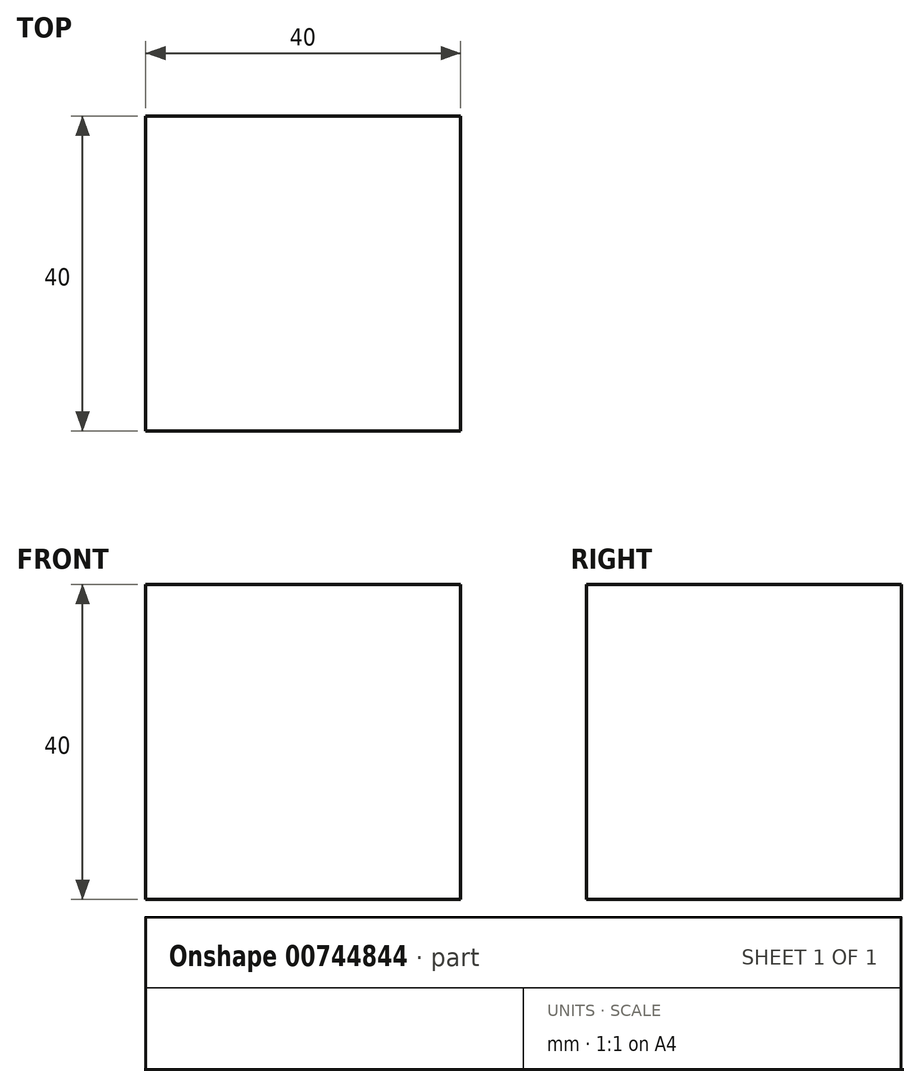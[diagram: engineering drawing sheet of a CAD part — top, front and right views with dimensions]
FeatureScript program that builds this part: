
annotation { "Feature Type Name" : "Feature", "Feature Type Description" : "" }
export const myFeature = defineFeature(function(context is Context, id is Id, definition is map)
    precondition{}
    {
        {
            var Q0;
            Q0=qCreatedBy(makeId("Top.planeOp"),FACE);
            var sketch = newSketch(context, id + "F0", { "sketchPlane" : qUnion([Q0])});
            skLineSegment(sketch, "E0.bottom", {"start": v(-17.96, 14.66) * mm, "end": v(22.04, 14.66) * mm});
            skLineSegment(sketch, "E0.top", {"start": v(-17.96, -25.34) * mm, "end": v(22.04, -25.34) * mm});
            skLineSegment(sketch, "E0.left", {"start": v(-17.96, 14.66) * mm, "end": v(-17.96, -25.34) * mm});
            skLineSegment(sketch, "E0.right", {"start": v(22.04, 14.66) * mm, "end": v(22.04, -25.34) * mm});
            skSolve(sketch);
        }
        {
            var Q0;
            Q0=makeQuery(id+"F0.imprint","IMPRINT",FACE,{"disambiguationData":[TD([[makeQuery(id+"F0.imprint","IMPRINT",EDGE,{"derivedFrom":sQuery(id+"F0.wireOp",EDGE,"E0.bottom")}),-1.0]])]});
            extrude(context, id + "F1", {"entities" : qUnion([Q0]), "depth" : 40 * mm, "offsetDistance" : 25 * mm});
        }
    });
